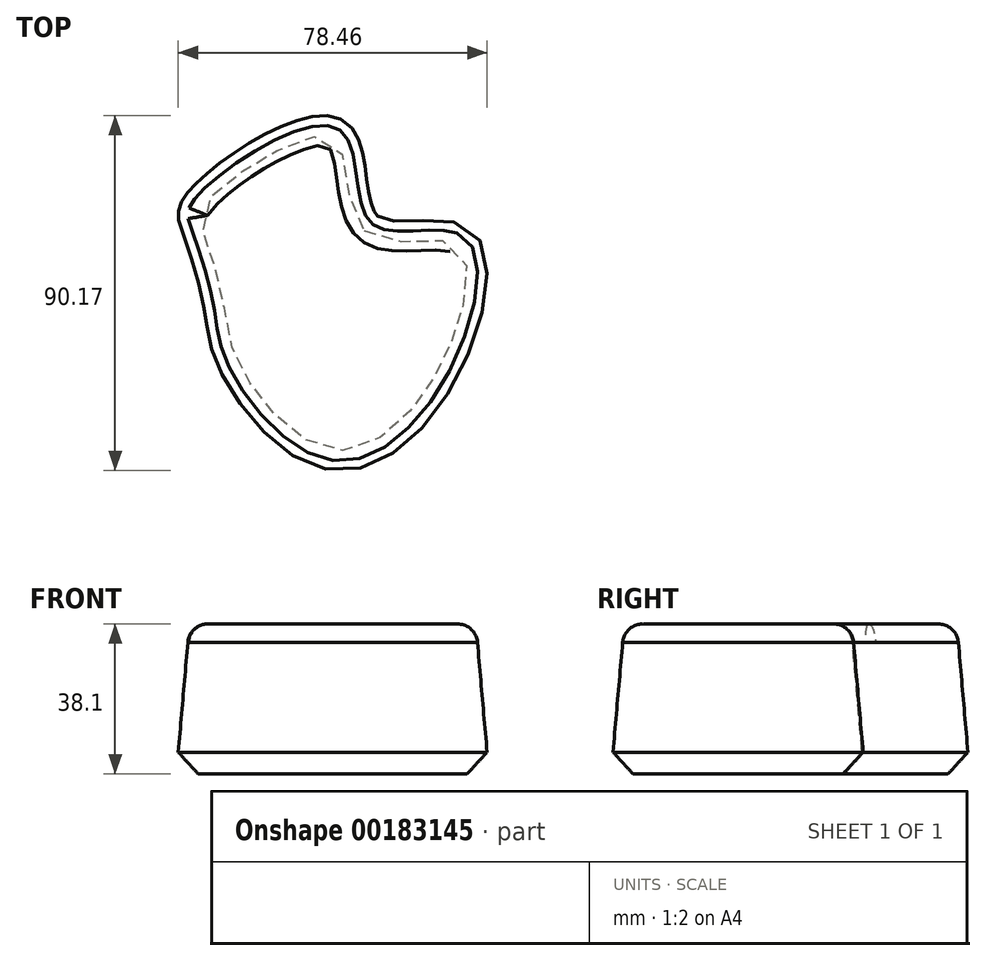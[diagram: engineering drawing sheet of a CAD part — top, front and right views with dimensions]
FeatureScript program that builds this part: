
annotation { "Feature Type Name" : "Feature", "Feature Type Description" : "" }
export const myFeature = defineFeature(function(context is Context, id is Id, definition is map)
    precondition{}
    {
        {
            var Q0;
            Q0=qCreatedBy(makeId("Top.planeOp"),FACE);
            var sketch = newSketch(context, id + "F0", { "sketchPlane" : qUnion([Q0])});
            skFitSpline(sketch, "E0", {"points": [v(-15.04, -8.06) * mm, v(9.73, -32.04) * mm, v(39.02, -12.58) * mm, v(44.13, 23.98) * mm, v(20.74, 27.33) * mm, v(12.29, 51.3) * mm, v(-23.5, 33.42) * mm, v(-24.08, 25.75) * mm, v(-18.77, 7.67) * mm, v(-15.04, -8.06) * mm]});
            skSolve(sketch);
        }
        {
            var Q0;
            Q0 = qSketchRegion(id + "F0", true);
            extrude(context, id + "F1", {"entities" : qUnion([Q0]), "oppositeDirection" : true, "depth" : 38.1 * mm, "hasDraft" : true, "draftAngle" : 5 * degree});
        }
        {
            var Q0;
            Q0=makeQuery(id+"F1.opExtrude","CAP_FACE",FACE,{"disambiguationData":[OSD([sQuery(id+"F0.wireOp",EDGE,"E0")])],"isStart":false});
            chamfer(context, id + "F2", {"entities" : qUnion([Q0]), "width" : 5.08 * mm, "tangentPropagation" : true});
        }
        {
            var Q0;
            Q0=makeQuery(id+"F1.opExtrude","CAP_EDGE",EDGE,{"disambiguationData":[OSD([sQuery(id+"F0.wireOp",EDGE,"E0")])],"isStart":true});
            fillet(context, id + "F3", {"entities" : qUnion([Q0]), "radius" : 5.08 * mm, "tangentPropagation" : true, "allowEdgeOverflow" : false});
        }
    });
